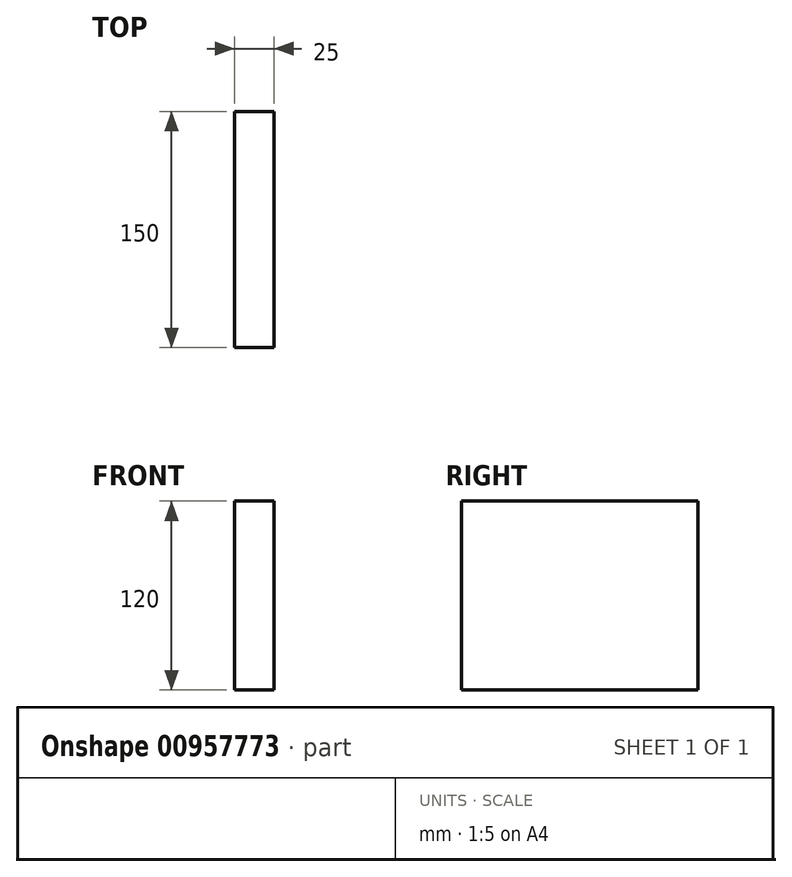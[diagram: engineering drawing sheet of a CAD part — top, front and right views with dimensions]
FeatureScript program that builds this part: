
annotation { "Feature Type Name" : "Feature", "Feature Type Description" : "" }
export const myFeature = defineFeature(function(context is Context, id is Id, definition is map)
    precondition{}
    {
        {
            var Q0;
            Q0=qCreatedBy(makeId("Right.planeOp"),FACE);
            var sketch = newSketch(context, id + "F0", { "sketchPlane" : qUnion([Q0])});
            skLineSegment(sketch, "E0.bottom", {"start": v(75, -60) * mm, "end": v(-75, -60) * mm});
            skLineSegment(sketch, "E0.top", {"start": v(75, 60) * mm, "end": v(-75, 60) * mm});
            skLineSegment(sketch, "E0.left", {"start": v(75, -60) * mm, "end": v(75, 60) * mm});
            skLineSegment(sketch, "E0.right", {"start": v(-75, -60) * mm, "end": v(-75, 60) * mm});
            skPoint(sketch, "E0.middle", {"position": v(0, 0) * mm});
            skSolve(sketch);
        }
        {
            var Q0;
            Q0=makeQuery(id+"F0.imprint","IMPRINT",FACE,{"disambiguationData":[TD([[makeQuery(id+"F0.imprint","IMPRINT",EDGE,{"derivedFrom":sQuery(id+"F0.wireOp",EDGE,"E0.bottom")}),-1.0]])]});
            extrude(context, id + "F1", {"entities" : qUnion([Q0]), "depth" : 25 * mm, "offsetDistance" : 25.4 * mm});
        }
    });
